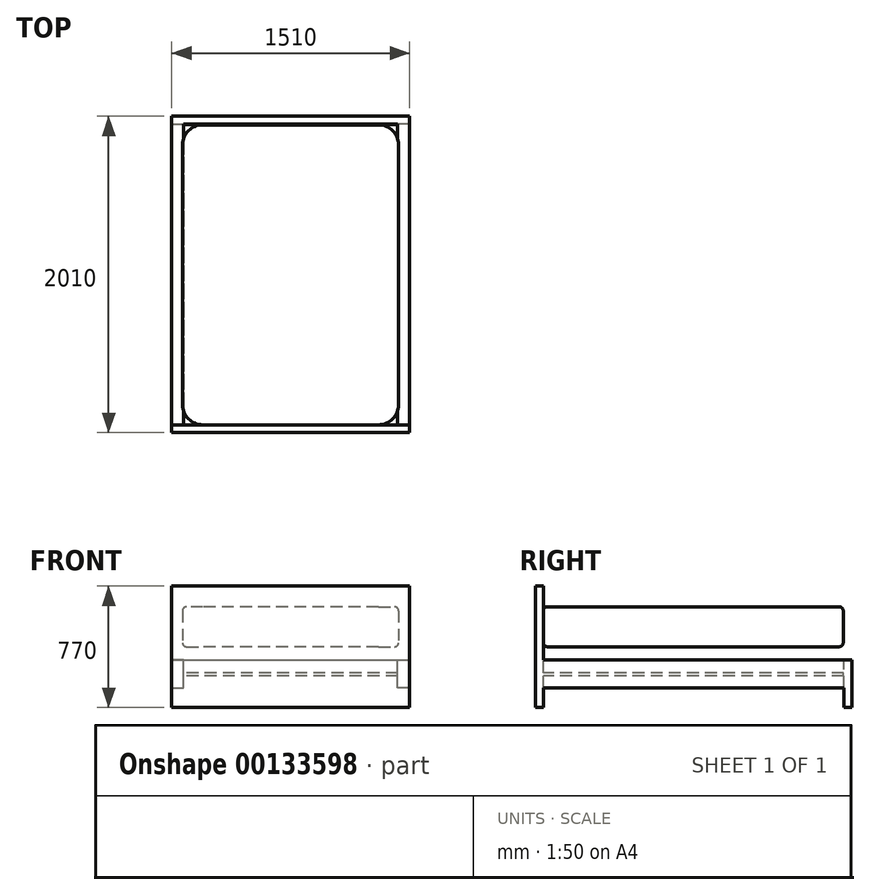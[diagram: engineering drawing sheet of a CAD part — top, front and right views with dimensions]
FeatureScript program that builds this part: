
annotation { "Feature Type Name" : "Feature", "Feature Type Description" : "" }
export const myFeature = defineFeature(function(context is Context, id is Id, definition is map)
    precondition{}
    {
        {
            var Q0;
            Q0=qCreatedBy(makeId("Top.planeOp"),FACE);
            var sketch = newSketch(context, id + "F0", { "sketchPlane" : qUnion([Q0])});
            skLineSegment(sketch, "E0.bottom", {"start": v(685.8, 952.5) * mm, "end": v(-685.8, 952.5) * mm});
            skLineSegment(sketch, "E0.top", {"start": v(685.8, -952.5) * mm, "end": v(-685.8, -952.5) * mm});
            skLineSegment(sketch, "E0.left", {"start": v(685.8, 952.5) * mm, "end": v(685.8, -952.5) * mm});
            skLineSegment(sketch, "E0.right", {"start": v(-685.8, 952.5) * mm, "end": v(-685.8, -952.5) * mm});
            skPoint(sketch, "E0.middle", {"position": v(0, 0) * mm});
            skSolve(sketch);
        }
        {
            var Q0;
            Q0=makeQuery(id+"F0.imprint","IMPRINT",FACE,{"disambiguationData":[TD([[makeQuery(id+"F0.imprint","IMPRINT",EDGE,{"derivedFrom":sQuery(id+"F0.wireOp",EDGE,"E0.bottom")}),1.0]])]});
            extrude(context, id + "F1", {"entities" : qUnion([Q0]), "depth" : 254 * mm});
        }
        {
            var Q0;
            Q0=makeQuery(id+"F1.opExtrude","CAP_EDGE",EDGE,{"disambiguationData":[OSD([sQuery(id+"F0.wireOp",EDGE,"E0.right")])],"isStart":false});
            var Q1;
            Q1=makeQuery(id+"F1.opExtrude","CAP_EDGE",EDGE,{"disambiguationData":[OSD([sQuery(id+"F0.wireOp",EDGE,"E0.bottom")])],"isStart":false});
            var Q2;
            Q2=makeQuery(id+"F1.opExtrude","CAP_EDGE",EDGE,{"disambiguationData":[OSD([sQuery(id+"F0.wireOp",EDGE,"E0.left")])],"isStart":false});
            var Q3;
            Q3=makeQuery(id+"F1.opExtrude","CAP_EDGE",EDGE,{"disambiguationData":[OSD([sQuery(id+"F0.wireOp",EDGE,"E0.top")])],"isStart":false});
            var Q4;
            Q4=makeQuery(id+"F1.opExtrude","CAP_EDGE",EDGE,{"disambiguationData":[OSD([sQuery(id+"F0.wireOp",EDGE,"E0.left")])],"isStart":true});
            var Q5;
            Q5=makeQuery(id+"F1.opExtrude","CAP_EDGE",EDGE,{"disambiguationData":[OSD([sQuery(id+"F0.wireOp",EDGE,"E0.bottom")])],"isStart":true});
            var Q6;
            Q6=makeQuery(id+"F1.opExtrude","CAP_EDGE",EDGE,{"disambiguationData":[OSD([sQuery(id+"F0.wireOp",EDGE,"E0.right")])],"isStart":true});
            var Q7;
            Q7=makeQuery(id+"F1.opExtrude","CAP_EDGE",EDGE,{"disambiguationData":[OSD([sQuery(id+"F0.wireOp",EDGE,"E0.top")])],"isStart":true});
            fillet(context, id + "F2", {"entities" : qUnion([Q0, Q1, Q2, Q3, Q4, Q5, Q6, Q7]), "radius" : 25.4 * mm, "tangentPropagation" : true, "allowEdgeOverflow" : false});
        }
        {
            var Q0;
            Q0=makeQuery(id+"F1.opExtrude","SWEPT_EDGE",EDGE,{"disambiguationData":[OSD([sQuery(id+"F0.wireOp",EDGE,"E0.top"),sQuery(id+"F0.wireOp",EDGE,"E0.left")])]});
            var Q1;
            Q1=makeQuery(id+"F1.opExtrude","SWEPT_EDGE",EDGE,{"disambiguationData":[OSD([sQuery(id+"F0.wireOp",EDGE,"E0.bottom"),sQuery(id+"F0.wireOp",EDGE,"E0.left")])]});
            var Q2;
            Q2=makeQuery(id+"F1.opExtrude","SWEPT_EDGE",EDGE,{"disambiguationData":[OSD([sQuery(id+"F0.wireOp",EDGE,"E0.bottom"),sQuery(id+"F0.wireOp",EDGE,"E0.right")])]});
            var Q3;
            Q3=makeQuery(id+"F1.opExtrude","SWEPT_EDGE",EDGE,{"disambiguationData":[OSD([sQuery(id+"F0.wireOp",EDGE,"E0.top"),sQuery(id+"F0.wireOp",EDGE,"E0.right")])]});
            fillet(context, id + "F3", {"entities" : qUnion([Q0, Q1, Q2, Q3]), "radius" : 127 * mm, "tangentPropagation" : true, "allowEdgeOverflow" : false});
        }
        {
            var Q0;
            Q0=makeQuery(id+"F1.opExtrude","SWEPT_FACE",FACE,{"disambiguationData":[OSD([sQuery(id+"F0.wireOp",EDGE,"E0.top")])]});
            var sketch = newSketch(context, id + "F4", { "sketchPlane" : qUnion([Q0])});
            skLineSegment(sketch, "E1.bottom", {"start": v(755, 385) * mm, "end": v(-755, 385) * mm});
            skLineSegment(sketch, "E1.top", {"start": v(755, -385) * mm, "end": v(-755, -385) * mm});
            skLineSegment(sketch, "E1.left", {"start": v(755, 385) * mm, "end": v(755, -385) * mm});
            skLineSegment(sketch, "E1.right", {"start": v(-755, 385) * mm, "end": v(-755, -385) * mm});
            skPoint(sketch, "E1.middle", {"position": v(0, 0) * mm});
            skSolve(sketch);
        }
        {
            var Q0;
            Q0=makeQuery(id+"F4.imprint","IMPRINT",FACE,{"disambiguationData":[TD([[makeQuery(id+"F4.imprint","IMPRINT",EDGE,{"derivedFrom":sQuery(id+"F4.wireOp",EDGE,"E1.bottom")}),1.0]])]});
            var Q1;
            {var subQ0=sQuery(id+"F0.wireOp",EDGE,"E0.top");var subQ1=makeQuery(id+"F1.opExtrude","SWEPT_FACE",FACE,{"disambiguationData":[OSD([subQ0])]});Q1=makeQuery(id+"F4.imprint","IMPRINT",FACE,{"disambiguationData":[TD([[makeQuery(id+"F4.imprint","IMPRINT",EDGE,{"derivedFrom":makeQuery(id+"F2.opFillet","BLEND_EDGE",EDGE,{"blendedFrom":[makeQuery(id+"F1.opExtrude","CAP_EDGE",EDGE,{"disambiguationData":[OSD([subQ0])],"isStart":true}),subQ1],"blendedInto":[subQ1]})}),1.0]])]});}
            extrude(context, id + "F5", {"entities" : qUnion([Q0, Q1]), "depth" : 50 * mm});
        }
        {
            var Q0;
            Q0=makeQuery(id+"F5.opExtrude","CAP_FACE",FACE,{"disambiguationData":[OSD([sQuery(id+"F4.wireOp",EDGE,"E1.bottom"),sQuery(id+"F4.wireOp",EDGE,"E1.top"),sQuery(id+"F4.wireOp",EDGE,"E1.left"),sQuery(id+"F4.wireOp",EDGE,"E1.right")])],"isStart":true});
            var sketch = newSketch(context, id + "F6", { "sketchPlane" : qUnion([Q0])});
            skLineSegment(sketch, "E2", {"start": v(0, -385) * mm, "end": v(0, -85) * mm, "construction": true});
            skLineSegment(sketch, "E3", {"start": v(0, -85) * mm, "end": v(755, -85) * mm, "construction": true});
            skLineSegment(sketch, "E4", {"start": v(755, -85) * mm, "end": v(755, -260) * mm});
            skLineSegment(sketch, "E5", {"start": v(755, -260) * mm, "end": v(680, -260) * mm});
            skLineSegment(sketch, "E6", {"start": v(680, -260) * mm, "end": v(680, -85) * mm});
            skLineSegment(sketch, "E7", {"start": v(680, -85) * mm, "end": v(755, -85) * mm});
            skLineSegment(sketch, "E8.MirrorCS", {"start": v(-755, -260) * mm, "end": v(-680, -260) * mm});
            skLineSegment(sketch, "E9.MirrorCS", {"start": v(-680, -260) * mm, "end": v(-680, -85) * mm});
            skLineSegment(sketch, "E10.MirrorCS", {"start": v(-755, -85) * mm, "end": v(-755, -260) * mm});
            skLineSegment(sketch, "E11", {"start": v(-680, -85) * mm, "end": v(-755, -85) * mm});
            skSolve(sketch);
        }
        {
            var Q0;
            Q0=makeQuery(id+"F6.imprint","IMPRINT",FACE,{"disambiguationData":[TD([[makeQuery(id+"F6.imprint","IMPRINT",EDGE,{"derivedFrom":sQuery(id+"F6.wireOp",EDGE,"E8.MirrorCS")}),1.0]])]});
            var Q1;
            Q1=makeQuery(id+"F6.imprint","IMPRINT",FACE,{"disambiguationData":[TD([[makeQuery(id+"F6.imprint","IMPRINT",EDGE,{"derivedFrom":sQuery(id+"F6.wireOp",EDGE,"E4")}),-1.0]])]});
            extrude(context, id + "F7", {"entities" : qUnion([Q0, Q1]), "operationType" : NewBodyOperationType.ADD, "depth" : 1910 * mm});
        }
        {
            var Q0;
            Q0=makeQuery(id+"F7.opExtrude","CAP_FACE",FACE,{"disambiguationData":[OSD([sQuery(id+"F6.wireOp",EDGE,"E8.MirrorCS"),sQuery(id+"F6.wireOp",EDGE,"E9.MirrorCS"),sQuery(id+"F6.wireOp",EDGE,"E10.MirrorCS"),sQuery(id+"F6.wireOp",EDGE,"E11")])],"isStart":false});
            var sketch = newSketch(context, id + "F8", { "sketchPlane" : qUnion([Q0])});
            skLineSegment(sketch, "E12", {"start": v(-755, -85) * mm, "end": v(755, -85) * mm});
            skLineSegment(sketch, "E13", {"start": v(755, -85) * mm, "end": v(755, -385) * mm});
            skLineSegment(sketch, "E14", {"start": v(755, -385) * mm, "end": v(-755, -385) * mm});
            skLineSegment(sketch, "E15", {"start": v(-755, -385) * mm, "end": v(-755, -85) * mm});
            skSolve(sketch);
        }
        {
            var Q0;
            {var subQ4=makeQuery(id+"F7.opExtrude","CAP_EDGE",EDGE,{"disambiguationData":[OSD([sQuery(id+"F6.wireOp",EDGE,"E8.MirrorCS")])],"isStart":false});Q0=makeQuery(id+"F8.imprint","IMPRINT",FACE,{"disambiguationData":[TD([[makeQuery(id+"F8.imprint","IMPRINT",EDGE,{"derivedFrom":subQ4}),1.0]])]});}
            var Q1;
            {var subQ3=sQuery(id+"F8.wireOp",EDGE,"E13");Q1=makeQuery(id+"F8.imprint","IMPRINT",FACE,{"disambiguationData":[TD([[makeQuery(id+"F8.imprint","IMPRINT",EDGE,{"derivedFrom":subQ3}),-1.0]])]});}
            extrude(context, id + "F9", {"entities" : qUnion([Q0, Q1]), "operationType" : NewBodyOperationType.ADD, "depth" : 50 * mm});
        }
        {
            var Q0;
            Q0=makeQuery(id+"F9.boolean.opBoolean","MERGE",FACE,{"derivedFrom":[makeQuery(id+"F7.opExtrude","SWEPT_FACE",FACE,{"disambiguationData":[OSD([sQuery(id+"F6.wireOp",EDGE,"E7")])]}),makeQuery(id+"F7.opExtrude","SWEPT_FACE",FACE,{"disambiguationData":[OSD([sQuery(id+"F6.wireOp",EDGE,"E11")])]}),makeQuery(id+"F9.opExtrude","SWEPT_FACE",FACE,{"disambiguationData":[OSD([sQuery(id+"F8.wireOp",EDGE,"E12")])]})]});
            var sketch = newSketch(context, id + "F10", { "sketchPlane" : qUnion([Q0])});
            skLineSegment(sketch, "E16.bottom", {"start": v(-680, 955) * mm, "end": v(680, 955) * mm});
            skLineSegment(sketch, "E16.top", {"start": v(-680, -955) * mm, "end": v(680, -955) * mm});
            skLineSegment(sketch, "E16.left", {"start": v(-680, 955) * mm, "end": v(-680, -955) * mm});
            skLineSegment(sketch, "E16.right", {"start": v(680, 955) * mm, "end": v(680, -955) * mm});
            skPoint(sketch, "E16.middle", {"position": v(0, 0) * mm});
            skSolve(sketch);
        }
        {
            var Q0;
            {var subQ4=sQuery(id+"F10.wireOp",EDGE,"E16.bottom");Q0=makeQuery(id+"F10.imprint","IMPRINT",FACE,{"disambiguationData":[TD([[makeQuery(id+"F10.imprint","IMPRINT",EDGE,{"derivedFrom":subQ4}),-1.0]])]});}
            extrude(context, id + "F11", {"entities" : qUnion([Q0]), "operationType" : NewBodyOperationType.ADD, "oppositeDirection" : true, "depth" : 100 * mm, "hasSecondDirection" : true, "secondDirectionOppositeDirection" : true, "secondDirectionDepth" : 80 * mm});
        }
    });
